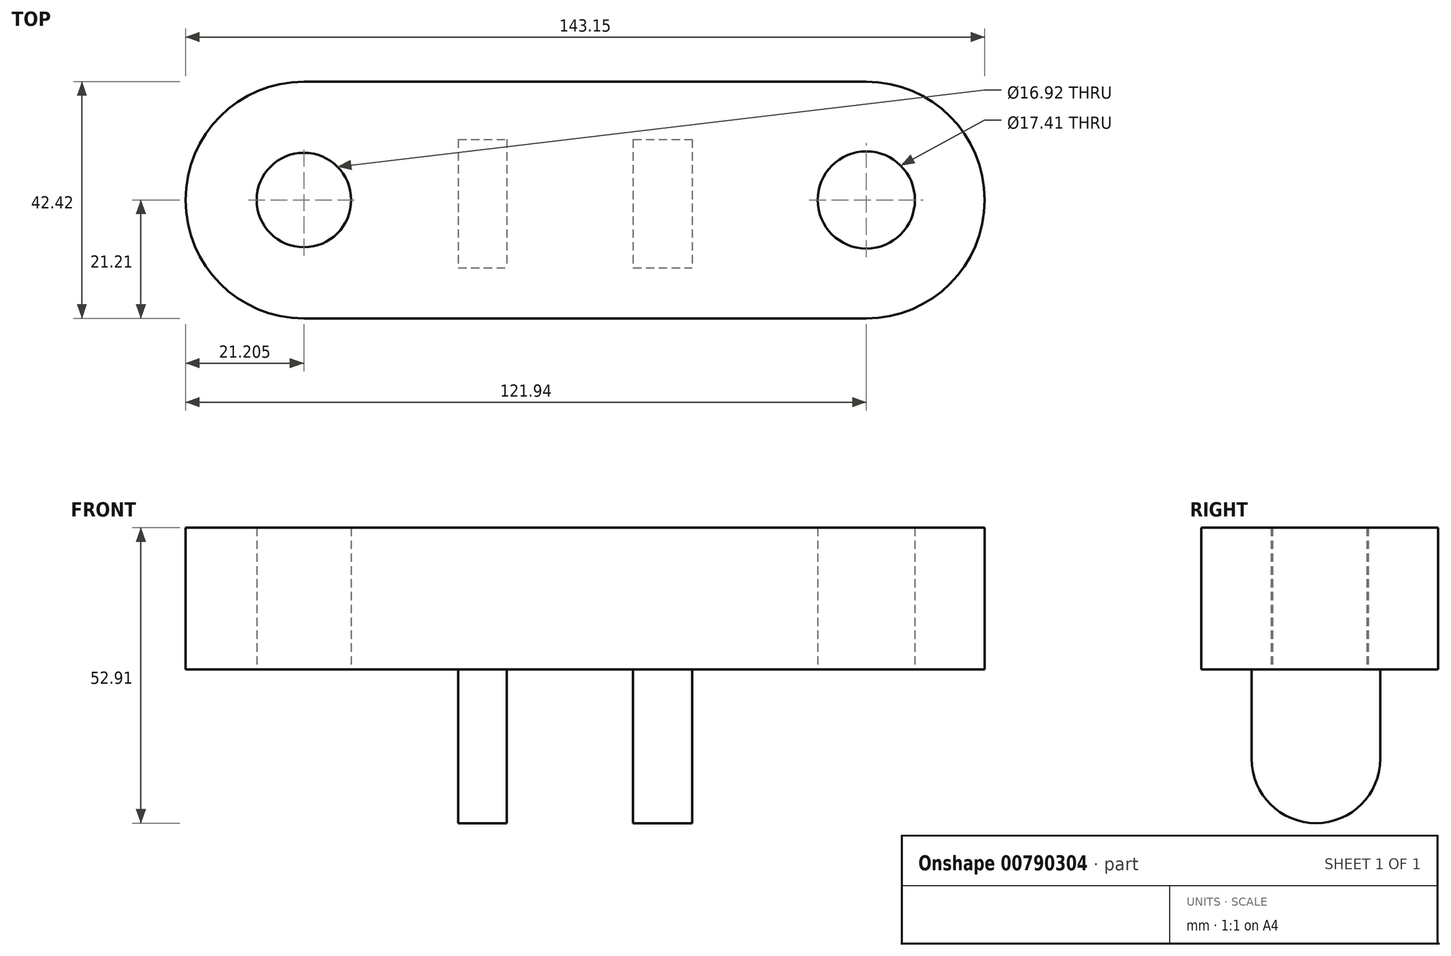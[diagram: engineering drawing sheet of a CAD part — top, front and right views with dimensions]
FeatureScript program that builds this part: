
annotation { "Feature Type Name" : "Feature", "Feature Type Description" : "" }
export const myFeature = defineFeature(function(context is Context, id is Id, definition is map)
    precondition{}
    {
        {
            var Q0;
            Q0=qCreatedBy(makeId("Top.planeOp"),FACE);
            var sketch = newSketch(context, id + "F0", { "sketchPlane" : qUnion([Q0])});
            skLineSegment(sketch, "E0.bottom", {"start": v(-42.54, 33.38) * mm, "end": v(58.2, 33.38) * mm});
            skLineSegment(sketch, "E0.top", {"start": v(-42.54, -9.04) * mm, "end": v(58.2, -9.04) * mm});
            skArc(sketch, "E1", {"start": v(-42.54, 33.38) * mm, "mid": v(-63.74, 12.17) * mm, "end": v(-42.54, -9.04) * mm});
            skArc(sketch, "E2", {"start": v(58.2, -9.04) * mm, "mid": v(79.4, 12.17) * mm, "end": v(58.2, 33.38) * mm});
            skCircle(sketch, "E3", {"center": v(-42.54, 12.17) * mm, "radius": 8.46 * mm});
            skCircle(sketch, "E4", {"center": v(58.2, 12.17) * mm, "radius": 8.7 * mm});
            skSolve(sketch);
        }
        {
            var Q0;
            Q0=makeQuery(id+"F0.imprint","IMPRINT",FACE,{"disambiguationData":[TD([[makeQuery(id+"F0.imprint","IMPRINT",EDGE,{"derivedFrom":sQuery(id+"F0.wireOp",EDGE,"E0.bottom")}),-1.0]])]});
            extrude(context, id + "F1", {"entities" : qUnion([Q0]), "depth" : 25.4 * mm, "offsetDistance" : 25.4 * mm});
        }
        {
            var Q0;
            Q0=qCreatedBy(makeId("Top.planeOp"),FACE);
            var sketch = newSketch(context, id + "F2", { "sketchPlane" : qUnion([Q0])});
            skLineSegment(sketch, "E5.bottom", {"start": v(-14.9, 23.01) * mm, "end": v(27.03, 23.01) * mm});
            skLineSegment(sketch, "E5.top", {"start": v(-14.9, 0) * mm, "end": v(27.03, 0) * mm});
            skLineSegment(sketch, "E5.left", {"start": v(-14.9, 23.01) * mm, "end": v(-14.9, 0) * mm});
            skLineSegment(sketch, "E5.right", {"start": v(27.03, 23.01) * mm, "end": v(27.03, 0) * mm});
            skLineSegment(sketch, "E6.bottom", {"start": v(-6.23, 23.01) * mm, "end": v(-14.9, 23.01) * mm});
            skLineSegment(sketch, "E6.top", {"start": v(-6.23, 0) * mm, "end": v(-14.9, 0) * mm});
            skLineSegment(sketch, "E6.left", {"start": v(-6.23, 23.01) * mm, "end": v(-6.23, 0) * mm});
            skLineSegment(sketch, "E7.bottom", {"start": v(16.42, 23.01) * mm, "end": v(27.03, 23.01) * mm});
            skLineSegment(sketch, "E7.top", {"start": v(16.42, 0) * mm, "end": v(27.03, 0) * mm});
            skLineSegment(sketch, "E7.left", {"start": v(16.42, 23.01) * mm, "end": v(16.42, 0) * mm});
            skSolve(sketch);
        }
        {
            var Q0;
            {var subQ2=sQuery(id+"F2.wireOp",EDGE,"E5.left");Q0=makeQuery(id+"F2.imprint","IMPRINT",FACE,{"disambiguationData":[TD([[makeQuery(id+"F2.imprint","IMPRINT",EDGE,{"derivedFrom":subQ2}),1.0]])]});}
            var Q1;
            {var subQ0=sQuery(id+"F2.wireOp",EDGE,"E5.right");Q1=makeQuery(id+"F2.imprint","IMPRINT",FACE,{"disambiguationData":[TD([[makeQuery(id+"F2.imprint","IMPRINT",EDGE,{"derivedFrom":subQ0}),-1.0]])]});}
            extrude(context, id + "F3", {"entities" : qUnion([Q0, Q1]), "operationType" : NewBodyOperationType.ADD, "oppositeDirection" : true, "depth" : 16 * mm, "offsetDistance" : 25.4 * mm});
        }
        {
            var Q0;
            Q0=makeQuery(id+"F3.opExtrude","CAP_FACE",FACE,{"disambiguationData":[OSD([sQuery(id+"F2.wireOp",EDGE,"E5.bottom"),sQuery(id+"F2.wireOp",EDGE,"E5.top"),sQuery(id+"F2.wireOp",EDGE,"E5.left"),sQuery(id+"F2.wireOp",EDGE,"E6.left")])],"isStart":false});
            var sketch = newSketch(context, id + "F4", { "sketchPlane" : qUnion([Q0])});
            skLineSegment(sketch, "E8", {"start": v(-14.9, -11.5) * mm, "end": v(-6.23, -11.5) * mm});
            skSolve(sketch);
        }
        {
            var Q0;
            Q0 = qSketchRegion(id + "F4", true);
            var Q1;
            {var subQ0=sQuery(id+"F4.wireOp",EDGE,"E8");Q1=makeQuery(id+"F4.imprint","IMPRINT",FACE,{"disambiguationData":[TD([[makeQuery(id+"F4.imprint","IMPRINT",EDGE,{"derivedFrom":subQ0}),1.0]])]});}
            var Q2;
            Q2=sQuery(id+"F4.wireOp",EDGE,"E8");
            revolve(context, id + "F5", {"operationType" : NewBodyOperationType.ADD, "surfaceOperationType" : NewSurfaceOperationType.NEW, "entities" : qUnion([Q0, Q1]), "axis" : qUnion([Q2]), "revolveType" : RevolveType.FULL});
        }
        {
            var Q0;
            Q0=makeQuery(id+"F3.opExtrude","CAP_FACE",FACE,{"disambiguationData":[OSD([sQuery(id+"F2.wireOp",EDGE,"E5.bottom"),sQuery(id+"F2.wireOp",EDGE,"E5.top"),sQuery(id+"F2.wireOp",EDGE,"E5.right"),sQuery(id+"F2.wireOp",EDGE,"E7.left")])],"isStart":false});
            var sketch = newSketch(context, id + "F6", { "sketchPlane" : qUnion([Q0])});
            skLineSegment(sketch, "E9", {"start": v(16.42, -11.5) * mm, "end": v(27.03, -11.5) * mm});
            skSolve(sketch);
        }
        {
            var Q0;
            Q0 = qSketchRegion(id + "F6", true);
            var Q1;
            {var subQ0=sQuery(id+"F6.wireOp",EDGE,"E9");Q1=makeQuery(id+"F6.imprint","IMPRINT",FACE,{"disambiguationData":[TD([[makeQuery(id+"F6.imprint","IMPRINT",EDGE,{"derivedFrom":subQ0}),1.0]])]});}
            var Q2;
            Q2=sQuery(id+"F6.wireOp",EDGE,"E9");
            revolve(context, id + "F7", {"operationType" : NewBodyOperationType.ADD, "surfaceOperationType" : NewSurfaceOperationType.NEW, "entities" : qUnion([Q0, Q1]), "axis" : qUnion([Q2]), "revolveType" : RevolveType.FULL});
        }
    });
